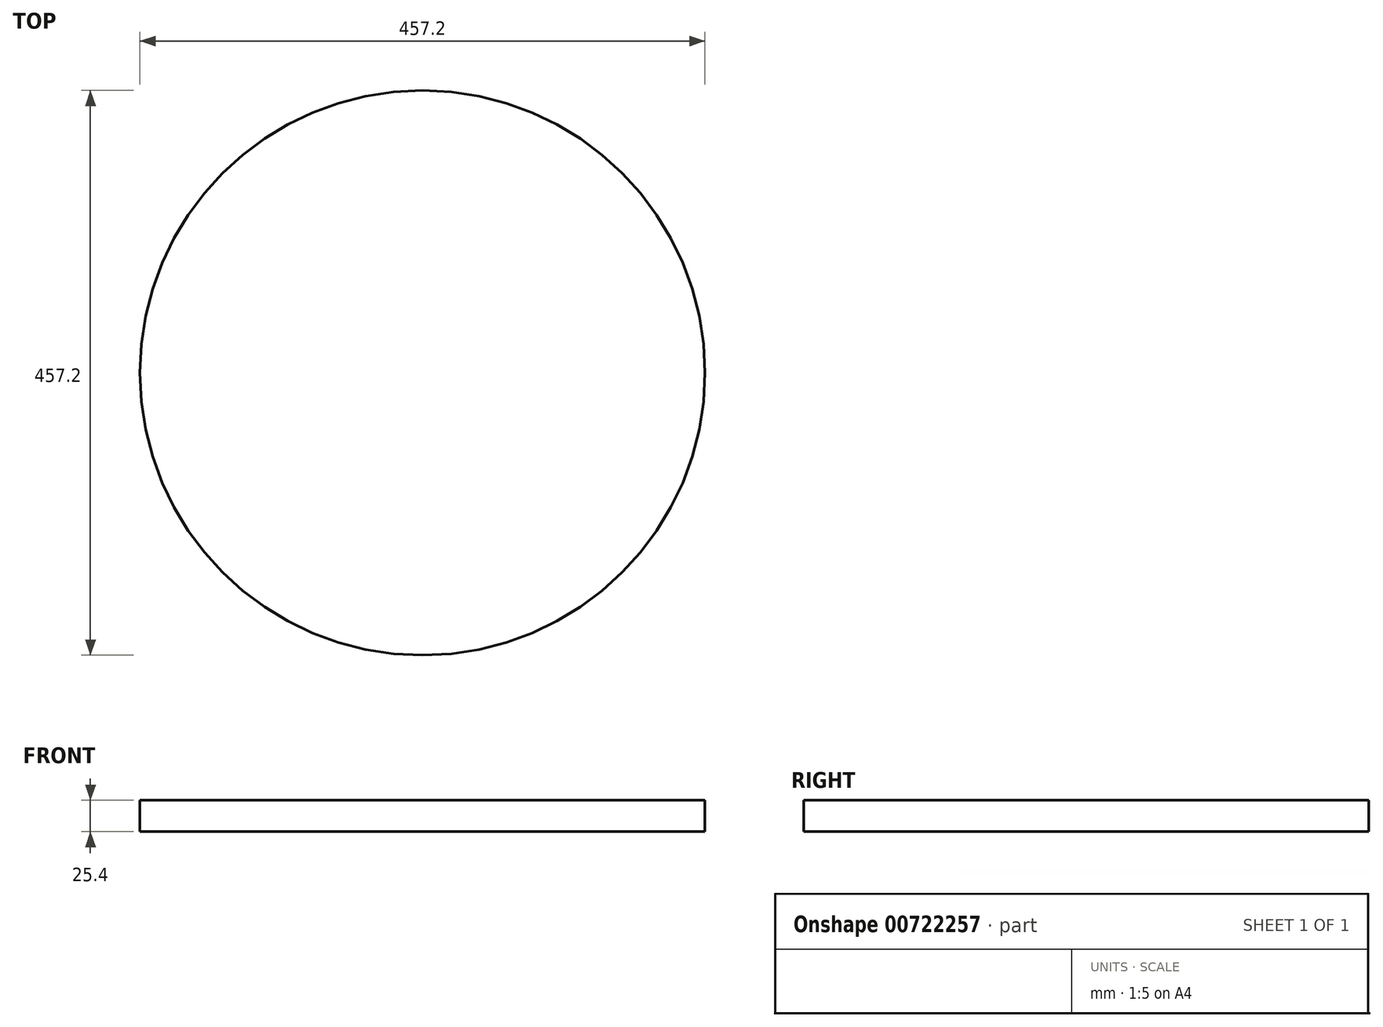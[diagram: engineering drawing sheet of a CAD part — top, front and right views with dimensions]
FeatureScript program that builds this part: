
annotation { "Feature Type Name" : "Feature", "Feature Type Description" : "" }
export const myFeature = defineFeature(function(context is Context, id is Id, definition is map)
    precondition{}
    {
        {
            var Q0;
            Q0=qCreatedBy(makeId("Top.planeOp"),FACE);
            var sketch = newSketch(context, id + "F0", { "sketchPlane" : qUnion([Q0])});
            skCircle(sketch, "E0", {"center": v(0, 0) * mm, "radius": 228.6 * mm});
            skSolve(sketch);
        }
        {
            var Q0;
            Q0=makeQuery(id+"F0.imprint","IMPRINT",FACE,{"disambiguationData":[TD([[makeQuery(id+"F0.imprint","IMPRINT",EDGE,{"derivedFrom":sQuery(id+"F0.wireOp",EDGE,"E0")}),1.0]])]});
            extrude(context, id + "F1", {"entities" : qUnion([Q0]), "depth" : 25.4 * mm, "offsetDistance" : 25.4 * mm});
        }
    });
